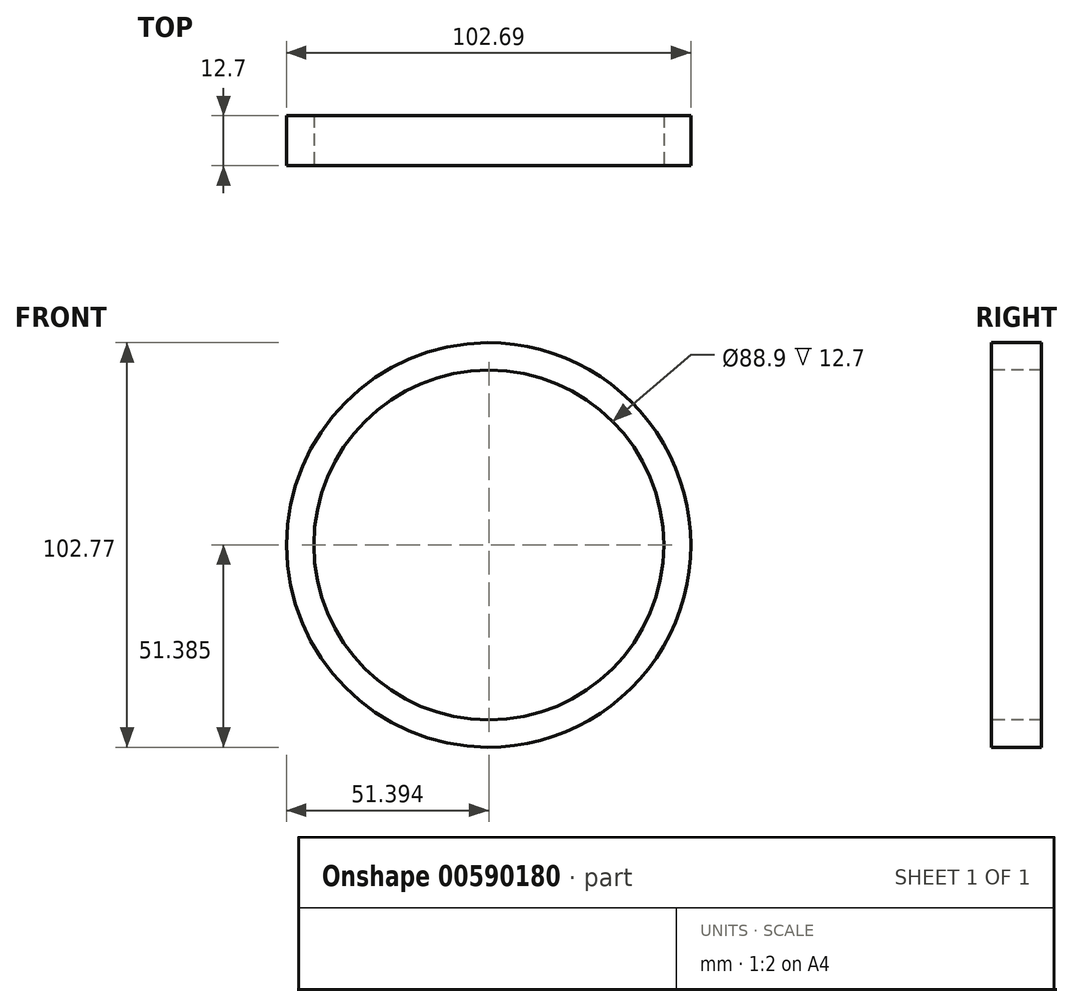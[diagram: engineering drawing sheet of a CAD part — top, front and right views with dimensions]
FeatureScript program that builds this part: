
annotation { "Feature Type Name" : "Feature", "Feature Type Description" : "" }
export const myFeature = defineFeature(function(context is Context, id is Id, definition is map)
    precondition{}
    {
        {
            var Q0;
            Q0=qCreatedBy(makeId("Front.planeOp"),FACE);
            var sketch = newSketch(context, id + "F0", { "sketchPlane" : qUnion([Q0])});
            skArc(sketch, "E0", {"start": v(6.6, -58.28) * mm, "mid": v(58.2, -6.9) * mm, "end": v(6.6, 44.5) * mm});
            skArc(sketch, "E1", {"start": v(6.6, 44.5) * mm, "mid": v(-44.49, -6.9) * mm, "end": v(6.6, -58.28) * mm});
            skSolve(sketch);
        }
        {
            var Q0;
            Q0=qSketchRegion(id+"F0",true);
            extrude(context, id + "F1", {"entities" : qUnion([Q0]), "depth" : 12.7 * mm, "offsetDistance" : 25.4 * mm});
        }
        {
            var Q0;
            Q0=makeQuery(id+"F1.opExtrude","CAP_FACE",FACE,{"disambiguationData":[OSD([sQuery(id+"F0.wireOp",EDGE,"E0"),sQuery(id+"F0.wireOp",EDGE,"E1")])],"isStart":false});
            var sketch = newSketch(context, id + "F2", { "sketchPlane" : qUnion([Q0])});
            skCircle(sketch, "E2", {"center": v(6.9, -6.9) * mm, "radius": 44.45 * mm});
            skSolve(sketch);
        }
        {
            var Q0;
            Q0=qSketchRegion(id+"F2",true);
            extrude(context, id + "F3", {"entities" : qUnion([Q0]), "operationType" : NewBodyOperationType.REMOVE, "oppositeDirection" : true, "depth" : 25.4 * mm, "offsetDistance" : 25.4 * mm});
        }
    });
